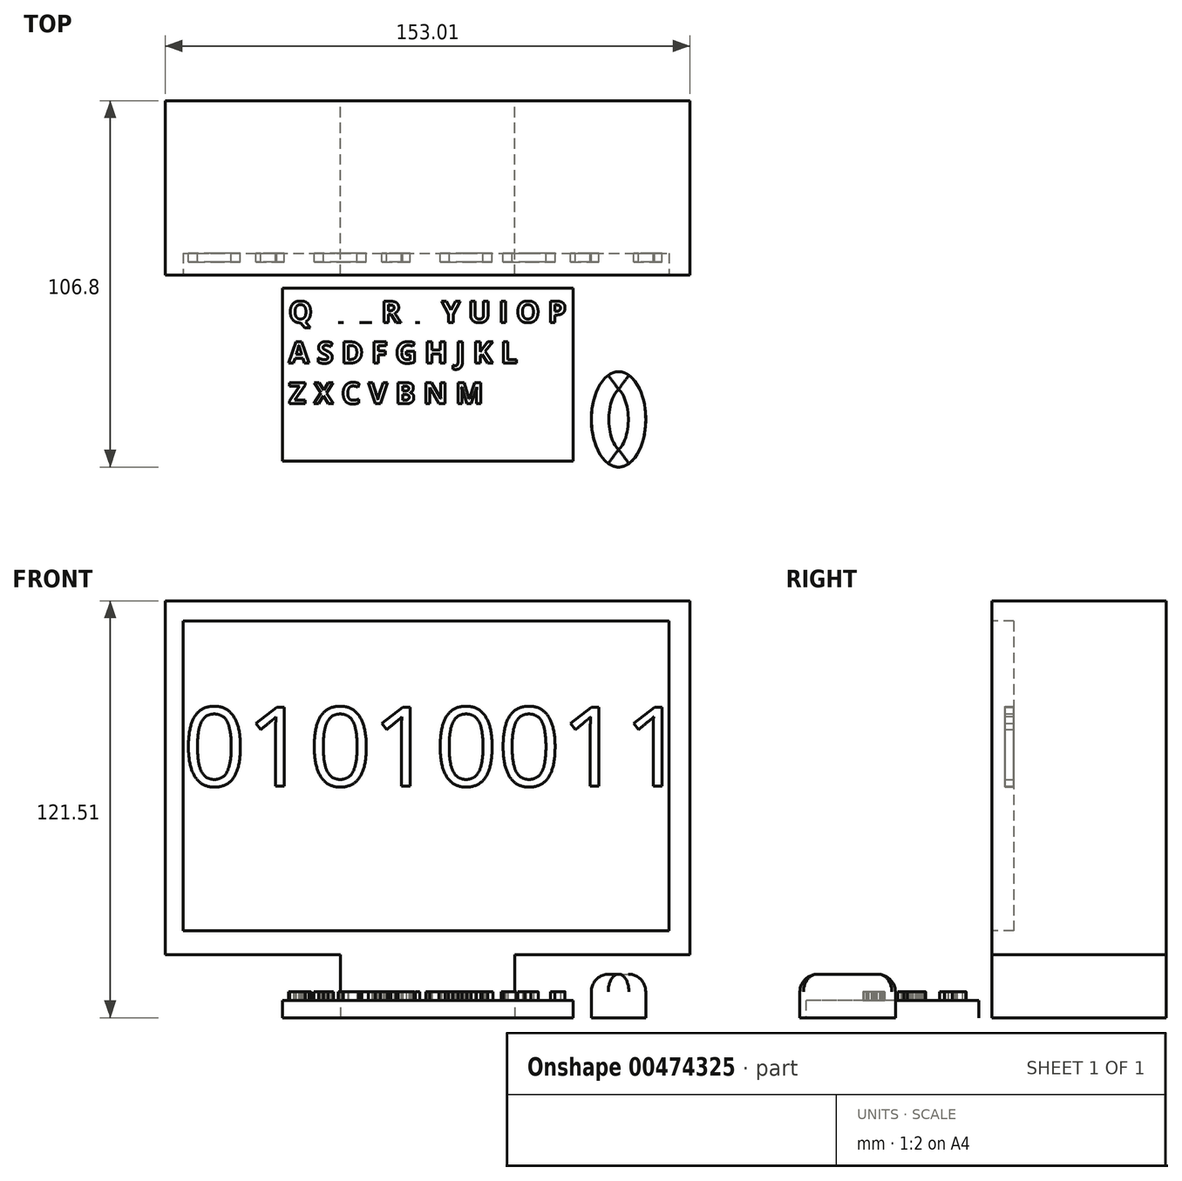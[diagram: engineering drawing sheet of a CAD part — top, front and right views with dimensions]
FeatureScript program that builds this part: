
annotation { "Feature Type Name" : "Feature", "Feature Type Description" : "" }
export const myFeature = defineFeature(function(context is Context, id is Id, definition is map)
    precondition{}
    {
        {
            var Q0;
            Q0=qCreatedBy(makeId("Top.planeOp"),FACE);
            var sketch = newSketch(context, id + "F0", { "sketchPlane" : qUnion([Q0])});
            skLineSegment(sketch, "E0.bottom", {"start": v(25.4, -25.4) * mm, "end": v(-25.4, -25.4) * mm});
            skLineSegment(sketch, "E0.top", {"start": v(25.4, 25.4) * mm, "end": v(-25.4, 25.4) * mm});
            skLineSegment(sketch, "E0.left", {"start": v(25.4, -25.4) * mm, "end": v(25.4, 25.4) * mm});
            skLineSegment(sketch, "E0.right", {"start": v(-25.4, -25.4) * mm, "end": v(-25.4, 25.4) * mm});
            skPoint(sketch, "E0.middle", {"position": v(0, 0) * mm});
            skSolve(sketch);
        }
        {
            var Q0;
            Q0 = qSketchRegion(id + "F0", true);
            extrude(context, id + "F1", {"entities" : qUnion([Q0]), "depth" : 25.4 * mm});
        }
        {
            var Q0;
            Q0=qCreatedBy(makeId("Front.planeOp"),FACE);
            var sketch = newSketch(context, id + "F2", { "sketchPlane" : qUnion([Q0])});
            skLineSegment(sketch, "E1.bottom", {"start": v(-76.56, 18.4) * mm, "end": v(76.45, 18.4) * mm});
            skLineSegment(sketch, "E1.top", {"start": v(-76.56, 121.5) * mm, "end": v(76.45, 121.5) * mm});
            skLineSegment(sketch, "E1.left", {"start": v(-76.56, 18.4) * mm, "end": v(-76.56, 121.5) * mm});
            skLineSegment(sketch, "E1.right", {"start": v(76.45, 18.4) * mm, "end": v(76.45, 121.5) * mm});
            skSolve(sketch);
        }
        {
            var Q0;
            Q0=makeQuery(id+"F2.imprint","IMPRINT",FACE,{"disambiguationData":[TD([[makeQuery(id+"F2.imprint","IMPRINT",EDGE,{"derivedFrom":sQuery(id+"F2.wireOp",EDGE,"E1.bottom")}),1.0]])]});
            extrude(context, id + "F3", {"entities" : qUnion([Q0]), "operationType" : NewBodyOperationType.ADD, "depth" : 25.4 * mm});
        }
        {
            var Q0;
            Q0=makeQuery(id+"F3.opExtrude","CAP_FACE",FACE,{"disambiguationData":[OSD([sQuery(id+"F2.wireOp",EDGE,"E1.bottom"),sQuery(id+"F2.wireOp",EDGE,"E1.top"),sQuery(id+"F2.wireOp",EDGE,"E1.left"),sQuery(id+"F2.wireOp",EDGE,"E1.right")])],"isStart":true});
            extrude(context, id + "F4", {"entities" : qUnion([Q0]), "operationType" : NewBodyOperationType.ADD, "depth" : 25.4 * mm});
        }
        {
            var Q0;
            Q0=makeQuery(id+"F3.boolean.opBoolean","MERGE",FACE,{"derivedFrom":[makeQuery(id+"F1.opExtrude","SWEPT_FACE",FACE,{"disambiguationData":[OSD([sQuery(id+"F0.wireOp",EDGE,"E0.bottom")])]}),makeQuery(id+"F3.opExtrude","CAP_FACE",FACE,{"disambiguationData":[OSD([sQuery(id+"F2.wireOp",EDGE,"E1.bottom"),sQuery(id+"F2.wireOp",EDGE,"E1.top"),sQuery(id+"F2.wireOp",EDGE,"E1.left"),sQuery(id+"F2.wireOp",EDGE,"E1.right")])],"isStart":false})]});
            var sketch = newSketch(context, id + "F5", { "sketchPlane" : qUnion([Q0])});
            skLineSegment(sketch, "E2.bottom", {"start": v(-71.36, 115.62) * mm, "end": v(70.34, 115.62) * mm});
            skLineSegment(sketch, "E2.top", {"start": v(-71.36, 25.36) * mm, "end": v(70.34, 25.36) * mm});
            skLineSegment(sketch, "E2.left", {"start": v(-71.36, 115.62) * mm, "end": v(-71.36, 25.36) * mm});
            skLineSegment(sketch, "E2.right", {"start": v(70.34, 115.62) * mm, "end": v(70.34, 25.36) * mm});
            skSolve(sketch);
        }
        {
            var Q0;
            Q0=makeQuery(id+"F5.imprint","IMPRINT",FACE,{"disambiguationData":[TD([[makeQuery(id+"F5.imprint","IMPRINT",EDGE,{"derivedFrom":sQuery(id+"F5.wireOp",EDGE,"E2.bottom")}),-1.0]])]});
            extrude(context, id + "F6", {"entities" : qUnion([Q0]), "operationType" : NewBodyOperationType.REMOVE, "oppositeDirection" : true, "depth" : 6.35 * mm});
        }
        {
            var Q0;
            Q0=qCreatedBy(makeId("Top.planeOp"),FACE);
            var sketch = newSketch(context, id + "F7", { "sketchPlane" : qUnion([Q0])});
            skEllipse(sketch, "E3", {"center": v(55.6, -67.49) * mm, "majorRadius": 13.91 * mm, "minorRadius": 7.91 * mm, "majorAxis": v(0, 1)});
            skSolve(sketch);
        }
        {
            var Q0;
            Q0=makeQuery(id+"F7.imprint","IMPRINT",FACE,{"disambiguationData":[TD([[makeQuery(id+"F7.imprint","IMPRINT",EDGE,{"derivedFrom":sQuery(id+"F7.wireOp",EDGE,"E3")}),1.0]])]});
            var Q1;
            Q1=sQuery(id+"F7.wireOp",EDGE,"E3");
            extrude(context, id + "F8", {"entities" : qUnion([Q0]), "surfaceEntities" : qUnion([Q1]), "depth" : 12.7 * mm});
        }
        {
            var Q0;
            Q0=makeQuery(id+"F8.opExtrude","CAP_EDGE",EDGE,{"disambiguationData":[OSD([sQuery(id+"F7.wireOp",EDGE,"E3")])],"isStart":false});
            fillet(context, id + "F9", {"entities" : qUnion([Q0]), "radius" : 5.08 * mm, "tangentPropagation" : true, "allowEdgeOverflow" : false});
        }
        {
            var Q0;
            Q0=qCreatedBy(makeId("Top.planeOp"),FACE);
            var sketch = newSketch(context, id + "F10", { "sketchPlane" : qUnion([Q0])});
            skLineSegment(sketch, "E4.bottom", {"start": v(-42.31, -29.26) * mm, "end": v(42.31, -29.26) * mm});
            skLineSegment(sketch, "E4.top", {"start": v(-42.31, -79.63) * mm, "end": v(42.31, -79.63) * mm});
            skLineSegment(sketch, "E4.left", {"start": v(-42.31, -29.26) * mm, "end": v(-42.31, -79.63) * mm});
            skLineSegment(sketch, "E4.right", {"start": v(42.31, -29.26) * mm, "end": v(42.31, -79.63) * mm});
            skPoint(sketch, "E4.middle", {"position": v(0, -54.44) * mm});
            skSolve(sketch);
        }
        {
            var Q0;
            Q0=makeQuery(id+"F10.imprint","IMPRINT",FACE,{"disambiguationData":[TD([[makeQuery(id+"F10.imprint","IMPRINT",EDGE,{"derivedFrom":sQuery(id+"F10.wireOp",EDGE,"E4.bottom")}),-1.0]])]});
            extrude(context, id + "F11", {"entities" : qUnion([Q0]), "depth" : 5.08 * mm});
        }
        {
            var Q0;
            Q0=makeQuery(id+"F11.opExtrude","CAP_FACE",FACE,{"disambiguationData":[OSD([sQuery(id+"F10.wireOp",EDGE,"E4.bottom"),sQuery(id+"F10.wireOp",EDGE,"E4.top"),sQuery(id+"F10.wireOp",EDGE,"E4.left"),sQuery(id+"F10.wireOp",EDGE,"E4.right")])],"isStart":false});
            var sketch = newSketch(context, id + "F12", { "sketchPlane" : qUnion([Q0])});
            skLineSegment(sketch, "E5.bottom", {"start": v(-40.56, -32.99) * mm, "end": v(40.56, -32.99) * mm});
            skLineSegment(sketch, "E5.top", {"start": v(-40.56, -39.26) * mm, "end": v(40.56, -39.26) * mm});
            skLineSegment(sketch, "E5.left", {"start": v(-40.56, -32.99) * mm, "end": v(-40.56, -39.26) * mm});
            skLineSegment(sketch, "E5.right", {"start": v(40.56, -32.99) * mm, "end": v(40.56, -39.26) * mm});
            skPoint(sketch, "E5.middle", {"position": v(0, -36.12) * mm});
            skText(sketch, "E6", { "text": "Q W E R T  Y U I O P\nA S D F G H J K L\nZ X C V B N M", "fontName": "OpenSans-Bold.ttf"});
            const initialGuessF12  = {"E6": [-0.04056, -0.03926, 1, 0, 0.00627]};
            skSetInitialGuess(sketch, initialGuessF12);
            skSolve(sketch);
        }
        {
            var Q0;
            Q0=makeQuery(id+"F12.imprint","IMPRINT",FACE,{"disambiguationData":[TD([[makeQuery(id+"F12.imprint","IMPRINT",EDGE,{"derivedFrom":sQuery(id+"F12.wireOp",EDGE,"E6.sketch_text.stroke-139")}),-1.0]])]});
            var Q1;
            Q1=makeQuery(id+"F12.imprint","IMPRINT",FACE,{"disambiguationData":[TD([[makeQuery(id+"F12.imprint","IMPRINT",EDGE,{"derivedFrom":sQuery(id+"F12.wireOp",EDGE,"E6.sketch_text.stroke-151")}),-1.0]])]});
            var Q2;
            Q2=makeQuery(id+"F12.imprint","IMPRINT",FACE,{"disambiguationData":[TD([[makeQuery(id+"F12.imprint","IMPRINT",EDGE,{"derivedFrom":sQuery(id+"F12.wireOp",EDGE,"E6.sketch_text.stroke-179")}),-1.0]])]});
            var Q3;
            Q3=makeQuery(id+"F12.imprint","IMPRINT",FACE,{"disambiguationData":[TD([[makeQuery(id+"F12.imprint","IMPRINT",EDGE,{"derivedFrom":sQuery(id+"F12.wireOp",EDGE,"E6.sketch_text.stroke-191")}),-1.0]])]});
            var Q4;
            Q4=makeQuery(id+"F12.imprint","IMPRINT",FACE,{"disambiguationData":[TD([[makeQuery(id+"F12.imprint","IMPRINT",EDGE,{"derivedFrom":sQuery(id+"F12.wireOp",EDGE,"E6.sketch_text.stroke-201")}),-1.0]])]});
            var Q5;
            Q5=makeQuery(id+"F12.imprint","IMPRINT",FACE,{"disambiguationData":[TD([[makeQuery(id+"F12.imprint","IMPRINT",EDGE,{"derivedFrom":sQuery(id+"F12.wireOp",EDGE,"E6.sketch_text.stroke-220")}),-1.0]])]});
            var Q6;
            Q6=makeQuery(id+"F12.imprint","IMPRINT",FACE,{"disambiguationData":[TD([[makeQuery(id+"F12.imprint","IMPRINT",EDGE,{"derivedFrom":sQuery(id+"F12.wireOp",EDGE,"E6.sketch_text.stroke-232")}),-1.0]])]});
            var Q7;
            Q7=makeQuery(id+"F12.imprint","IMPRINT",FACE,{"disambiguationData":[TD([[makeQuery(id+"F12.imprint","IMPRINT",EDGE,{"derivedFrom":sQuery(id+"F12.wireOp",EDGE,"E6.sketch_text.stroke-242")}),-1.0]])]});
            var Q8;
            Q8=makeQuery(id+"F12.imprint","IMPRINT",FACE,{"disambiguationData":[TD([[makeQuery(id+"F12.imprint","IMPRINT",EDGE,{"derivedFrom":sQuery(id+"F12.wireOp",EDGE,"E6.sketch_text.stroke-255")}),-1.0]])]});
            extrude(context, id + "F13", {"entities" : qUnion([Q0, Q1, Q2, Q3, Q4, Q5, Q6, Q7, Q8]), "operationType" : NewBodyOperationType.ADD, "depth" : 2.54 * mm});
        }
        {
            var Q0;
            Q0=makeQuery(id+"F12.imprint","IMPRINT",FACE,{"disambiguationData":[TD([[makeQuery(id+"F12.imprint","IMPRINT",EDGE,{"derivedFrom":sQuery(id+"F12.wireOp",EDGE,"E6.sketch_text.stroke-123")}),-1.0]])]});
            var Q1;
            {var subQ11=sQuery(id+"F12.wireOp",EDGE,"E6.sketch_text.stroke-109");Q1=makeQuery(id+"F12.imprint","IMPRINT",FACE,{"disambiguationData":[TD([[makeQuery(id+"F12.imprint","IMPRINT",EDGE,{"derivedFrom":subQ11}),-1.0]])]});}
            var Q2;
            Q2=makeQuery(id+"F12.imprint","IMPRINT",FACE,{"disambiguationData":[TD([[makeQuery(id+"F12.imprint","IMPRINT",EDGE,{"derivedFrom":sQuery(id+"F12.wireOp",EDGE,"E6.sketch_text.stroke-105")}),-1.0]])]});
            var Q3;
            Q3=makeQuery(id+"F12.imprint","IMPRINT",FACE,{"disambiguationData":[TD([[makeQuery(id+"F12.imprint","IMPRINT",EDGE,{"derivedFrom":sQuery(id+"F12.wireOp",EDGE,"E6.sketch_text.stroke-90")}),-1.0]])]});
            var Q4;
            Q4=makeQuery(id+"F12.imprint","IMPRINT",FACE,{"disambiguationData":[TD([[makeQuery(id+"F12.imprint","IMPRINT",EDGE,{"derivedFrom":sQuery(id+"F12.wireOp",EDGE,"E6.sketch_text.stroke-81")}),-1.0]])]});
            var Q5;
            Q5=makeQuery(id+"F12.imprint","IMPRINT",FACE,{"disambiguationData":[TD([[makeQuery(id+"F12.imprint","IMPRINT",EDGE,{"derivedFrom":sQuery(id+"F12.wireOp",EDGE,"E6.sketch_text.stroke-73")}),-1.0]])]});
            var Q6;
            Q6=makeQuery(id+"F12.imprint","IMPRINT",FACE,{"disambiguationData":[TD([[makeQuery(id+"F12.imprint","IMPRINT",EDGE,{"derivedFrom":sQuery(id+"F12.wireOp",EDGE,"E6.sketch_text.stroke-54")}),-1.0]])]});
            var Q7;
            Q7=makeQuery(id+"F12.imprint","IMPRINT",FACE,{"disambiguationData":[TD([[makeQuery(id+"F12.imprint","IMPRINT",EDGE,{"derivedFrom":sQuery(id+"F12.wireOp",EDGE,"E6.sketch_text.stroke-42")}),-1.0]])]});
            var Q8;
            Q8=makeQuery(id+"F12.imprint","IMPRINT",FACE,{"disambiguationData":[TD([[makeQuery(id+"F12.imprint","IMPRINT",EDGE,{"derivedFrom":sQuery(id+"F12.wireOp",EDGE,"E6.sketch_text.stroke-18")}),-1.0]])]});
            var Q9;
            Q9=makeQuery(id+"F12.imprint","IMPRINT",FACE,{"disambiguationData":[TD([[makeQuery(id+"F12.imprint","IMPRINT",EDGE,{"derivedFrom":sQuery(id+"F12.wireOp",EDGE,"E6.sketch_text.stroke-0")}),-1.0]])]});
            var Q10;
            {var subQ5=sQuery(id+"F12.wireOp",EDGE,"E6.sketch_text.stroke-3");Q10=makeQuery(id+"F12.imprint","IMPRINT",FACE,{"disambiguationData":[TD([[makeQuery(id+"F12.imprint","IMPRINT",EDGE,{"derivedFrom":subQ5}),-1.0]])]});}
            extrude(context, id + "F14", {"entities" : qUnion([Q0, Q1, Q2, Q3, Q4, Q5, Q6, Q7, Q8, Q9, Q10]), "operationType" : NewBodyOperationType.ADD, "depth" : 2.54 * mm});
        }
        {
            var Q0;
            Q0=makeQuery(id+"F12.imprint","IMPRINT",FACE,{"disambiguationData":[TD([[makeQuery(id+"F12.imprint","IMPRINT",EDGE,{"derivedFrom":sQuery(id+"F12.wireOp",EDGE,"E6.sketch_text.stroke-261")}),-1.0]])]});
            var Q1;
            Q1=makeQuery(id+"F12.imprint","IMPRINT",FACE,{"disambiguationData":[TD([[makeQuery(id+"F12.imprint","IMPRINT",EDGE,{"derivedFrom":sQuery(id+"F12.wireOp",EDGE,"E6.sketch_text.stroke-271")}),-1.0]])]});
            var Q2;
            Q2=makeQuery(id+"F12.imprint","IMPRINT",FACE,{"disambiguationData":[TD([[makeQuery(id+"F12.imprint","IMPRINT",EDGE,{"derivedFrom":sQuery(id+"F12.wireOp",EDGE,"E6.sketch_text.stroke-283")}),-1.0]])]});
            var Q3;
            Q3=makeQuery(id+"F12.imprint","IMPRINT",FACE,{"disambiguationData":[TD([[makeQuery(id+"F12.imprint","IMPRINT",EDGE,{"derivedFrom":sQuery(id+"F12.wireOp",EDGE,"E6.sketch_text.stroke-298")}),-1.0]])]});
            var Q4;
            Q4=makeQuery(id+"F12.imprint","IMPRINT",FACE,{"disambiguationData":[TD([[makeQuery(id+"F12.imprint","IMPRINT",EDGE,{"derivedFrom":sQuery(id+"F12.wireOp",EDGE,"E6.sketch_text.stroke-308")}),-1.0]])]});
            var Q5;
            Q5=makeQuery(id+"F12.imprint","IMPRINT",FACE,{"disambiguationData":[TD([[makeQuery(id+"F12.imprint","IMPRINT",EDGE,{"derivedFrom":sQuery(id+"F12.wireOp",EDGE,"E6.sketch_text.stroke-333")}),-1.0]])]});
            var Q6;
            Q6=makeQuery(id+"F12.imprint","IMPRINT",FACE,{"disambiguationData":[TD([[makeQuery(id+"F12.imprint","IMPRINT",EDGE,{"derivedFrom":sQuery(id+"F12.wireOp",EDGE,"E6.sketch_text.stroke-347")}),-1.0]])]});
            extrude(context, id + "F15", {"entities" : qUnion([Q0, Q1, Q2, Q3, Q4, Q5, Q6]), "operationType" : NewBodyOperationType.ADD, "depth" : 2.54 * mm});
        }
        {
            var Q0;
            Q0=makeQuery(id+"F6.boolean.opBoolean","COPY",FACE,{"derivedFrom":makeQuery(id+"F6.opExtrude","CAP_FACE",FACE,{"disambiguationData":[OSD([sQuery(id+"F5.wireOp",EDGE,"E2.bottom"),sQuery(id+"F5.wireOp",EDGE,"E2.top"),sQuery(id+"F5.wireOp",EDGE,"E2.left"),sQuery(id+"F5.wireOp",EDGE,"E2.right")])],"isStart":false})});
            var sketch = newSketch(context, id + "F16", { "sketchPlane" : qUnion([Q0])});
            skText(sketch, "E7", { "text": "01010011 ", "fontName": "OpenSans-Regular.ttf"});
            const initialGuessF16  = {"E7": [-0.07136, 0.06754, 1, 0, 0.0231]};
            skSetInitialGuess(sketch, initialGuessF16);
            skSolve(sketch);
        }
        {
            var Q0;
            Q0=makeQuery(id+"F16.imprint","IMPRINT",FACE,{"disambiguationData":[TD([[makeQuery(id+"F16.imprint","IMPRINT",EDGE,{"derivedFrom":sQuery(id+"F16.wireOp",EDGE,"E7.sketch_text.stroke-0")}),-1.0]])]});
            var Q1;
            Q1=makeQuery(id+"F16.imprint","IMPRINT",FACE,{"disambiguationData":[TD([[makeQuery(id+"F16.imprint","IMPRINT",EDGE,{"derivedFrom":sQuery(id+"F16.wireOp",EDGE,"E7.sketch_text.stroke-16")}),-1.0]])]});
            var Q2;
            Q2=makeQuery(id+"F16.imprint","IMPRINT",FACE,{"disambiguationData":[TD([[makeQuery(id+"F16.imprint","IMPRINT",EDGE,{"derivedFrom":sQuery(id+"F16.wireOp",EDGE,"E7.sketch_text.stroke-25")}),-1.0]])]});
            var Q3;
            Q3=makeQuery(id+"F16.imprint","IMPRINT",FACE,{"disambiguationData":[TD([[makeQuery(id+"F16.imprint","IMPRINT",EDGE,{"derivedFrom":sQuery(id+"F16.wireOp",EDGE,"E7.sketch_text.stroke-41")}),-1.0]])]});
            var Q4;
            Q4=makeQuery(id+"F16.imprint","IMPRINT",FACE,{"disambiguationData":[TD([[makeQuery(id+"F16.imprint","IMPRINT",EDGE,{"derivedFrom":sQuery(id+"F16.wireOp",EDGE,"E7.sketch_text.stroke-50")}),-1.0]])]});
            var Q5;
            Q5=makeQuery(id+"F16.imprint","IMPRINT",FACE,{"disambiguationData":[TD([[makeQuery(id+"F16.imprint","IMPRINT",EDGE,{"derivedFrom":sQuery(id+"F16.wireOp",EDGE,"E7.sketch_text.stroke-66")}),-1.0]])]});
            var Q6;
            Q6=makeQuery(id+"F16.imprint","IMPRINT",FACE,{"disambiguationData":[TD([[makeQuery(id+"F16.imprint","IMPRINT",EDGE,{"derivedFrom":sQuery(id+"F16.wireOp",EDGE,"E7.sketch_text.stroke-82")}),-1.0]])]});
            var Q7;
            Q7=makeQuery(id+"F16.imprint","IMPRINT",FACE,{"disambiguationData":[TD([[makeQuery(id+"F16.imprint","IMPRINT",EDGE,{"derivedFrom":sQuery(id+"F16.wireOp",EDGE,"E7.sketch_text.stroke-91")}),-1.0]])]});
            extrude(context, id + "F17", {"entities" : qUnion([Q0, Q1, Q2, Q3, Q4, Q5, Q6, Q7]), "operationType" : NewBodyOperationType.ADD, "depth" : 2.54 * mm});
        }
    });
